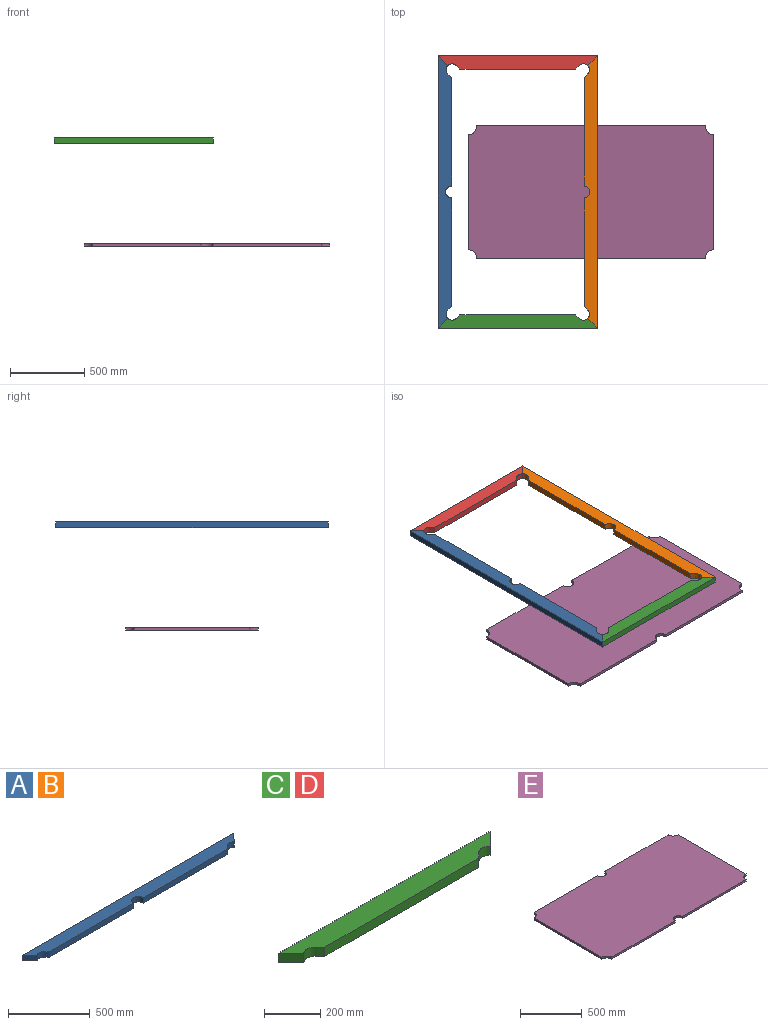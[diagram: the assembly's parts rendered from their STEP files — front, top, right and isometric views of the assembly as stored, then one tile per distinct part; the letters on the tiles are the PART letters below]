
ASSEMBLY  parts=5 mates=7
PART A: 12 faces, bbox 1830x90x40 mm
  f0: plane 728.43x40mm, normal (0,-1,0), area 29137.3mm2, adj f2,f3,f7,f11
  f1: plane 65.25x65.25mm, normal (0.71,-0.71,0), area 3691.2mm2, adj f2,f3,f4,f10
  f2: plane 1830x90mm, normal (0,0,1), area 150373.5mm2, adj f0,f1,f4,f5,f6,f7,f8,f9
  f3: plane 1830x90mm, normal (0,0,-1), area 150373.5mm2, adj f0,f1,f4,f5,f6,f7,f8,f9
  f4: plane 1830x40mm, normal (0,1,0), area 73200mm2, adj f1,f2,f3,f5
  f5: plane 65.25x65.25mm, normal (-0.71,-0.71,0), area 3691.2mm2, adj f2,f3,f4,f9
  f6: plane 728.43x40mm, normal (0,-1,0), area 29137.3mm2, adj f2,f3,f7,f8
  f7: cylinder r=40mm len=80mm, axis (0,0,1), area 5026.5mm2, adj f0,f2,f3,f6
  f8: plane 40x24.75mm, normal (-0.71,-0.71,0), area 1400mm2, adj f2,f3,f6,f9
  f9: cylinder r=40mm len=56.57mm, axis (0,0,1), area 2513.3mm2, adj f2,f3,f5,f8
  f10: cylinder r=40mm len=56.57mm, axis (0,0,1), area 2513.3mm2, adj f1,f2,f3,f11
  f11: plane 40x24.75mm, normal (0.71,-0.71,0), area 1400mm2, adj f0,f2,f3,f10
PART B: same geometry as A
PART C: 10 faces, bbox 1070x90x40 mm
  f0: plane 776.86x40mm, normal (0,-1,0), area 31074.5mm2, adj f2,f3,f7,f8
  f1: plane 65.25x65.25mm, normal (0.71,-0.71,0), area 3691.2mm2, adj f2,f3,f4,f6
  f2: plane 1070x90mm, normal (0,0,1), area 84486.7mm2, adj f0,f1,f4,f5,f6,f7,f8,f9
  f3: plane 1070x90mm, normal (0,0,-1), area 84486.7mm2, adj f0,f1,f4,f5,f6,f7,f8,f9
  f4: plane 1070x40mm, normal (0,1,0), area 42800mm2, adj f1,f2,f3,f5
  f5: plane 65.25x65.25mm, normal (-0.71,-0.71,0), area 3691.2mm2, adj f2,f3,f4,f9
  f6: cylinder r=40mm len=56.57mm, axis (0,0,1), area 2513.3mm2, adj f1,f2,f3,f7
  f7: plane 40x24.75mm, normal (0.71,-0.71,0), area 1400mm2, adj f0,f2,f3,f6
  f8: plane 40x24.75mm, normal (-0.71,-0.71,0), area 1400mm2, adj f0,f2,f3,f9
  f9: cylinder r=40mm len=56.57mm, axis (0,0,1), area 2513.3mm2, adj f2,f3,f5,f8
PART D: same geometry as C
PART E: 14 faces, bbox 1650x890x19 mm
  f0: plane 726.02x19mm, normal (0,-1,0), area 13794.3mm2, adj f1,f11,f12,f13
  f1: cylinder r=57.98mm len=57.98mm, axis (0,0,-1), area 1730.5mm2, adj f0,f2,f12,f13
  f2: plane 774.03x19mm, normal (1,0,0), area 14706.7mm2, adj f1,f3,f12,f13
  f3: cylinder r=57.98mm len=57.98mm, axis (0,0,-1), area 1730.5mm2, adj f2,f4,f12,f13
  f4: plane 726.02x19mm, normal (0,1,0), area 13794.3mm2, adj f3,f5,f12,f13
  f5: cylinder r=41mm len=82mm, axis (0,0,-1), area 2447.3mm2, adj f4,f6,f12,f13
  f6: plane 726.02x19mm, normal (0,1,0), area 13794.3mm2, adj f5,f7,f12,f13
  f7: cylinder r=57.98mm len=57.98mm, axis (0,0,-1), area 1730.5mm2, adj f6,f8,f12,f13
  f8: plane 774.03x19mm, normal (-1,0,0), area 14706.7mm2, adj f7,f9,f12,f13
  f9: cylinder r=57.98mm len=57.98mm, axis (0,0,-1), area 1730.5mm2, adj f8,f10,f12,f13
  f10: plane 726.02x19mm, normal (0,-1,0), area 13794.3mm2, adj f9,f11,f12,f13
  f11: cylinder r=41mm len=82mm, axis (0,0,-1), area 2447.3mm2, adj f0,f10,f12,f13
  f12: plane 1650x890mm, normal (0,0,1), area 1452656.9mm2, adj f0,f1,f2,f3,f4,f5,f6,f7
  f13: plane 1650x890mm, normal (0,0,-1), area 1452656.9mm2, adj f0,f1,f2,f3,f4,f5,f6,f7
PLACE A rot(axis=(0,0,1),90deg) t=(-1067.98,-767,1013.9)mm
PLACE B rot(axis=(0,0,-1),90deg) t=(2.02,-767,1013.9)mm
PLACE C rot(axis=(0,0,-1),180deg) t=(-532.98,-1682,1013.9)mm
PLACE D t=(-532.98,148,1013.9)mm
PLACE E t=(-41.01,-767,327.9)mm fixed
MATE slider C.f5 <-> B.f1  axis (0.71,0.71,0) through (-30.61,-1649.38,1033.9)mm
MATE slider E.f12 <-> B.f3  axis (0,0,1) through (-41.01,-767,346.9)mm
MATE slider A.f1 <-> D.f5  axis (0.71,0.71,0) through (-1035.36,115.37,1033.9)mm
MATE slider B.f5 <-> D.f1  axis (-0.71,0.71,0) through (-30.61,115.37,1033.9)mm
MATE fastened B.f2 <-> C.f2  axis (0,0,1) through (2.02,-1682,1053.9)mm
MATE fastened B.f2 <-> D.f2  axis (0,0,1) through (-63.24,82.74,1053.9)mm
MATE fastened A.f2 <-> D.f2  axis (0,0,1) through (-1067.98,148,1053.9)mm
